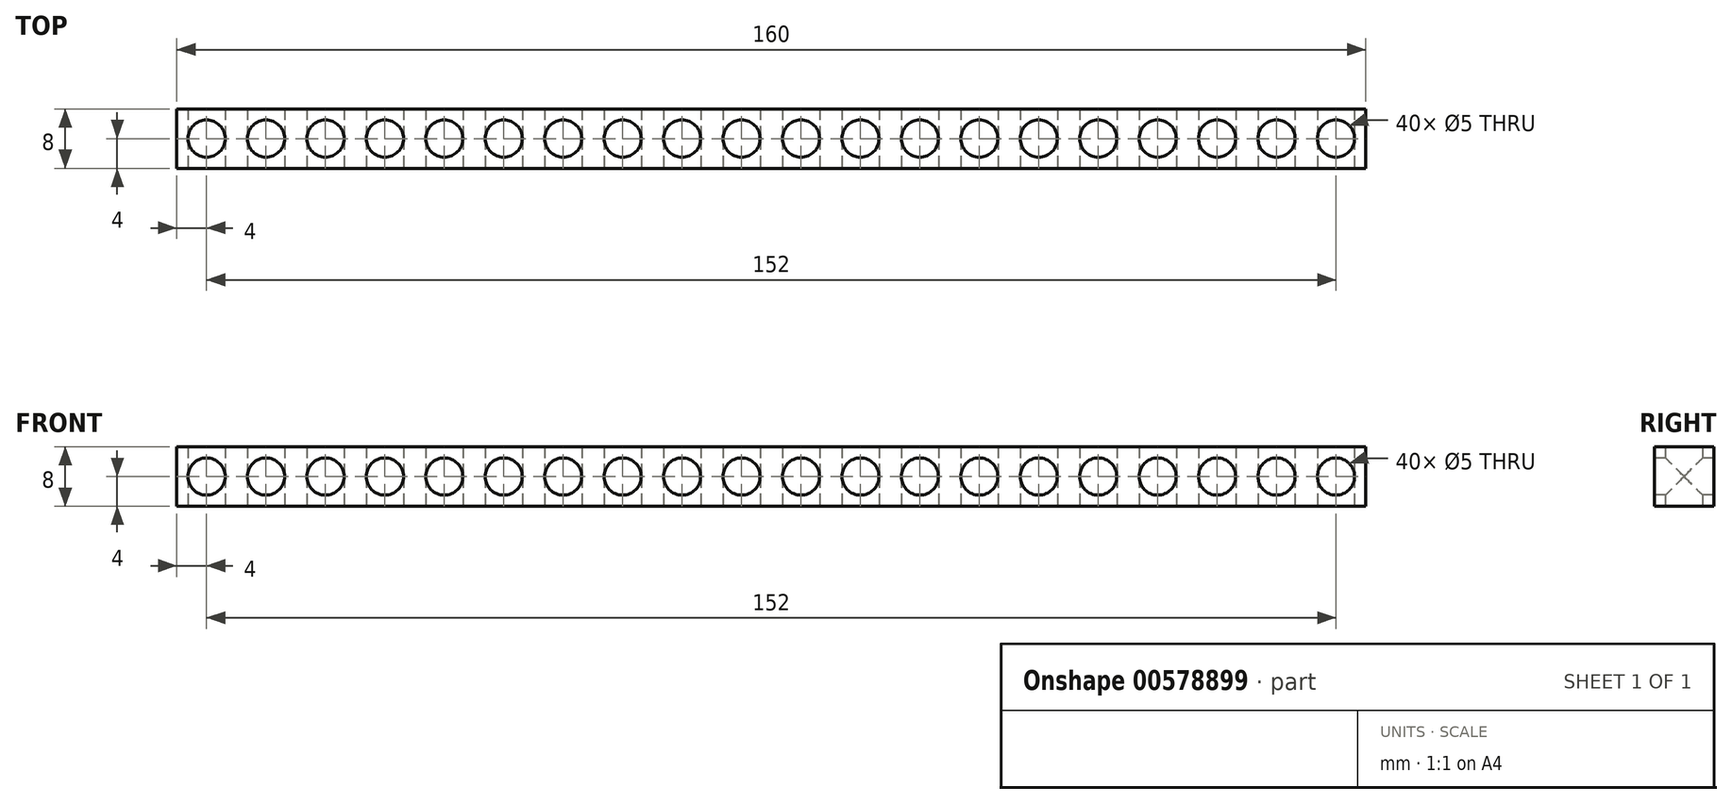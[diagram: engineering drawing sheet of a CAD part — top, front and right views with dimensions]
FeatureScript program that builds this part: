
annotation { "Feature Type Name" : "Feature", "Feature Type Description" : "" }
export const myFeature = defineFeature(function(context is Context, id is Id, definition is map)
    precondition{}
    {
        {
            var Q0;
            Q0=qCreatedBy(makeId("Top.planeOp"),FACE);
            var sketch = newSketch(context, id + "F0", { "sketchPlane" : qUnion([Q0])});
            skLineSegment(sketch, "E0.bottom", {"start": v(80, 4) * mm, "end": v(-80, 4) * mm});
            skLineSegment(sketch, "E0.top", {"start": v(80, -4) * mm, "end": v(-80, -4) * mm});
            skLineSegment(sketch, "E0.left", {"start": v(80, 4) * mm, "end": v(80, -4) * mm});
            skLineSegment(sketch, "E0.right", {"start": v(-80, 4) * mm, "end": v(-80, -4) * mm});
            skPoint(sketch, "E0.middle", {"position": v(0, 0) * mm});
            skLineSegment(sketch, "E1", {"start": v(-80, 0) * mm, "end": v(80, 0) * mm, "construction": true});
            skCircle(sketch, "E2", {"center": v(-76, 0) * mm, "radius": 2.5 * mm});
            skCircle(sketch, "E3.1.0.0", {"center": v(-68, 0) * mm, "radius": 2.5 * mm});
            skCircle(sketch, "E3.2.0.0", {"center": v(-60, 0) * mm, "radius": 2.5 * mm});
            skCircle(sketch, "E3.3.0.0", {"center": v(-52, 0) * mm, "radius": 2.5 * mm});
            skCircle(sketch, "E3.4.0.0", {"center": v(-44, 0) * mm, "radius": 2.5 * mm});
            skCircle(sketch, "E3.5.0.0", {"center": v(-36, 0) * mm, "radius": 2.5 * mm});
            skCircle(sketch, "E3.6.0.0", {"center": v(-28, 0) * mm, "radius": 2.5 * mm});
            skCircle(sketch, "E3.7.0.0", {"center": v(-20, 0) * mm, "radius": 2.5 * mm});
            skCircle(sketch, "E3.8.0.0", {"center": v(-12, 0) * mm, "radius": 2.5 * mm});
            skCircle(sketch, "E3.9.0.0", {"center": v(-4, 0) * mm, "radius": 2.5 * mm});
            skCircle(sketch, "E3.10.0.0", {"center": v(4, 0) * mm, "radius": 2.5 * mm});
            skCircle(sketch, "E3.11.0.0", {"center": v(12, 0) * mm, "radius": 2.5 * mm});
            skCircle(sketch, "E3.12.0.0", {"center": v(20, 0) * mm, "radius": 2.5 * mm});
            skCircle(sketch, "E3.13.0.0", {"center": v(28, 0) * mm, "radius": 2.5 * mm});
            skCircle(sketch, "E3.14.0.0", {"center": v(36, 0) * mm, "radius": 2.5 * mm});
            skCircle(sketch, "E3.15.0.0", {"center": v(44, 0) * mm, "radius": 2.5 * mm});
            skCircle(sketch, "E3.16.0.0", {"center": v(52, 0) * mm, "radius": 2.5 * mm});
            skCircle(sketch, "E3.17.0.0", {"center": v(60, 0) * mm, "radius": 2.5 * mm});
            skCircle(sketch, "E3.18.0.0", {"center": v(68, 0) * mm, "radius": 2.5 * mm});
            skCircle(sketch, "E3.19.0.0", {"center": v(76, 0) * mm, "radius": 2.5 * mm});
            skLineSegment(sketch, "E3.direction1", {"start": v(-76, 0) * mm, "end": v(-68, 0) * mm, "construction": true});
            skSolve(sketch);
        }
        {
            var Q0;
            Q0 = qSketchRegion(id + "F0", true);
            extrude(context, id + "F1", {"entities" : qUnion([Q0]), "endBound" : BoundingType.SYMMETRIC, "depth" : 8 * mm, "offsetDistance" : 25 * mm});
        }
        {
            var Q0;
            Q0=makeQuery(id+"F1.opExtrude","SWEPT_FACE",FACE,{"disambiguationData":[OSD([sQuery(id+"F0.wireOp",EDGE,"E0.top")])]});
            var sketch = newSketch(context, id + "F2", { "sketchPlane" : qUnion([Q0])});
            skLineSegment(sketch, "E4", {"start": v(-80, 0) * mm, "end": v(80, 0) * mm, "construction": true});
            skCircle(sketch, "E5", {"center": v(-76, 0) * mm, "radius": 2.5 * mm});
            skCircle(sketch, "E6.1.0.0", {"center": v(-68, 0) * mm, "radius": 2.5 * mm});
            skCircle(sketch, "E6.2.0.0", {"center": v(-60, 0) * mm, "radius": 2.5 * mm});
            skCircle(sketch, "E6.3.0.0", {"center": v(-52, 0) * mm, "radius": 2.5 * mm});
            skCircle(sketch, "E6.4.0.0", {"center": v(-44, 0) * mm, "radius": 2.5 * mm});
            skCircle(sketch, "E6.5.0.0", {"center": v(-36, 0) * mm, "radius": 2.5 * mm});
            skCircle(sketch, "E6.6.0.0", {"center": v(-28, 0) * mm, "radius": 2.5 * mm});
            skCircle(sketch, "E6.7.0.0", {"center": v(-20, 0) * mm, "radius": 2.5 * mm});
            skCircle(sketch, "E6.8.0.0", {"center": v(-12, 0) * mm, "radius": 2.5 * mm});
            skCircle(sketch, "E6.9.0.0", {"center": v(-4, 0) * mm, "radius": 2.5 * mm});
            skCircle(sketch, "E6.10.0.0", {"center": v(4, 0) * mm, "radius": 2.5 * mm});
            skCircle(sketch, "E6.11.0.0", {"center": v(12, 0) * mm, "radius": 2.5 * mm});
            skCircle(sketch, "E6.12.0.0", {"center": v(20, 0) * mm, "radius": 2.5 * mm});
            skCircle(sketch, "E6.13.0.0", {"center": v(28, 0) * mm, "radius": 2.5 * mm});
            skCircle(sketch, "E6.14.0.0", {"center": v(36, 0) * mm, "radius": 2.5 * mm});
            skCircle(sketch, "E6.15.0.0", {"center": v(44, 0) * mm, "radius": 2.5 * mm});
            skCircle(sketch, "E6.16.0.0", {"center": v(52, 0) * mm, "radius": 2.5 * mm});
            skCircle(sketch, "E6.17.0.0", {"center": v(60, 0) * mm, "radius": 2.5 * mm});
            skCircle(sketch, "E6.18.0.0", {"center": v(68, 0) * mm, "radius": 2.5 * mm});
            skCircle(sketch, "E6.19.0.0", {"center": v(76, 0) * mm, "radius": 2.5 * mm});
            skLineSegment(sketch, "E6.direction1", {"start": v(-76, 0) * mm, "end": v(-68, 0) * mm, "construction": true});
            skSolve(sketch);
        }
        {
            var Q0;
            Q0 = qSketchRegion(id + "F2", true);
            var Q1;
            Q1=makeQuery(id+"F1.opExtrude","SWEPT_FACE",FACE,{"disambiguationData":[OSD([sQuery(id+"F0.wireOp",EDGE,"E0.bottom")])]});
            extrude(context, id + "F3", {"entities" : qUnion([Q0]), "operationType" : NewBodyOperationType.REMOVE, "endBound" : BoundingType.UP_TO_SURFACE, "oppositeDirection" : true, "depth" : 25 * mm, "endBoundEntityFace" : qUnion([Q1]), "offsetDistance" : 25 * mm});
        }
    });
